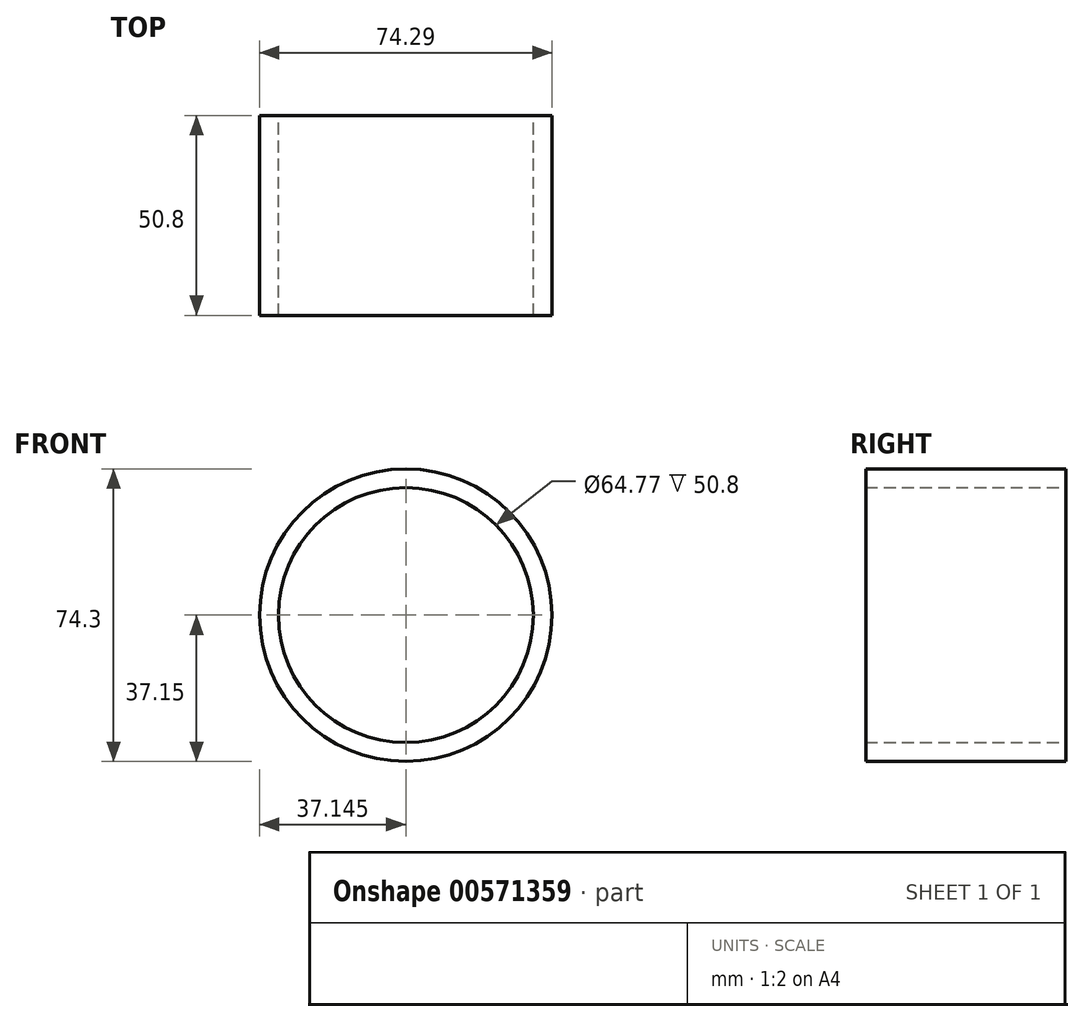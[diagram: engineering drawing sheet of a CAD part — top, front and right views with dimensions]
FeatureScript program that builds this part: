
annotation { "Feature Type Name" : "Feature", "Feature Type Description" : "" }
export const myFeature = defineFeature(function(context is Context, id is Id, definition is map)
    precondition{}
    {
        {
            var Q0;
            Q0=qCreatedBy(makeId("Front.planeOp"),FACE);
            var sketch = newSketch(context, id + "F0", { "sketchPlane" : qUnion([Q0])});
            skCircle(sketch, "E0", {"center": v(-56.45, 43.41) * mm, "radius": 37.15 * mm});
            skCircle(sketch, "E1", {"center": v(-56.45, 43.41) * mm, "radius": 32.39 * mm});
            skSolve(sketch);
        }
        {
            var Q0;
            Q0=makeQuery(id+"F0.imprint","IMPRINT",FACE,{"disambiguationData":[TD([[makeQuery(id+"F0.imprint","IMPRINT",EDGE,{"derivedFrom":sQuery(id+"F0.wireOp",EDGE,"E0")}),1.0]])]});
            extrude(context, id + "F1", {"entities" : qUnion([Q0]), "depth" : 50.8 * mm, "offsetDistance" : 25.4 * mm});
        }
    });
